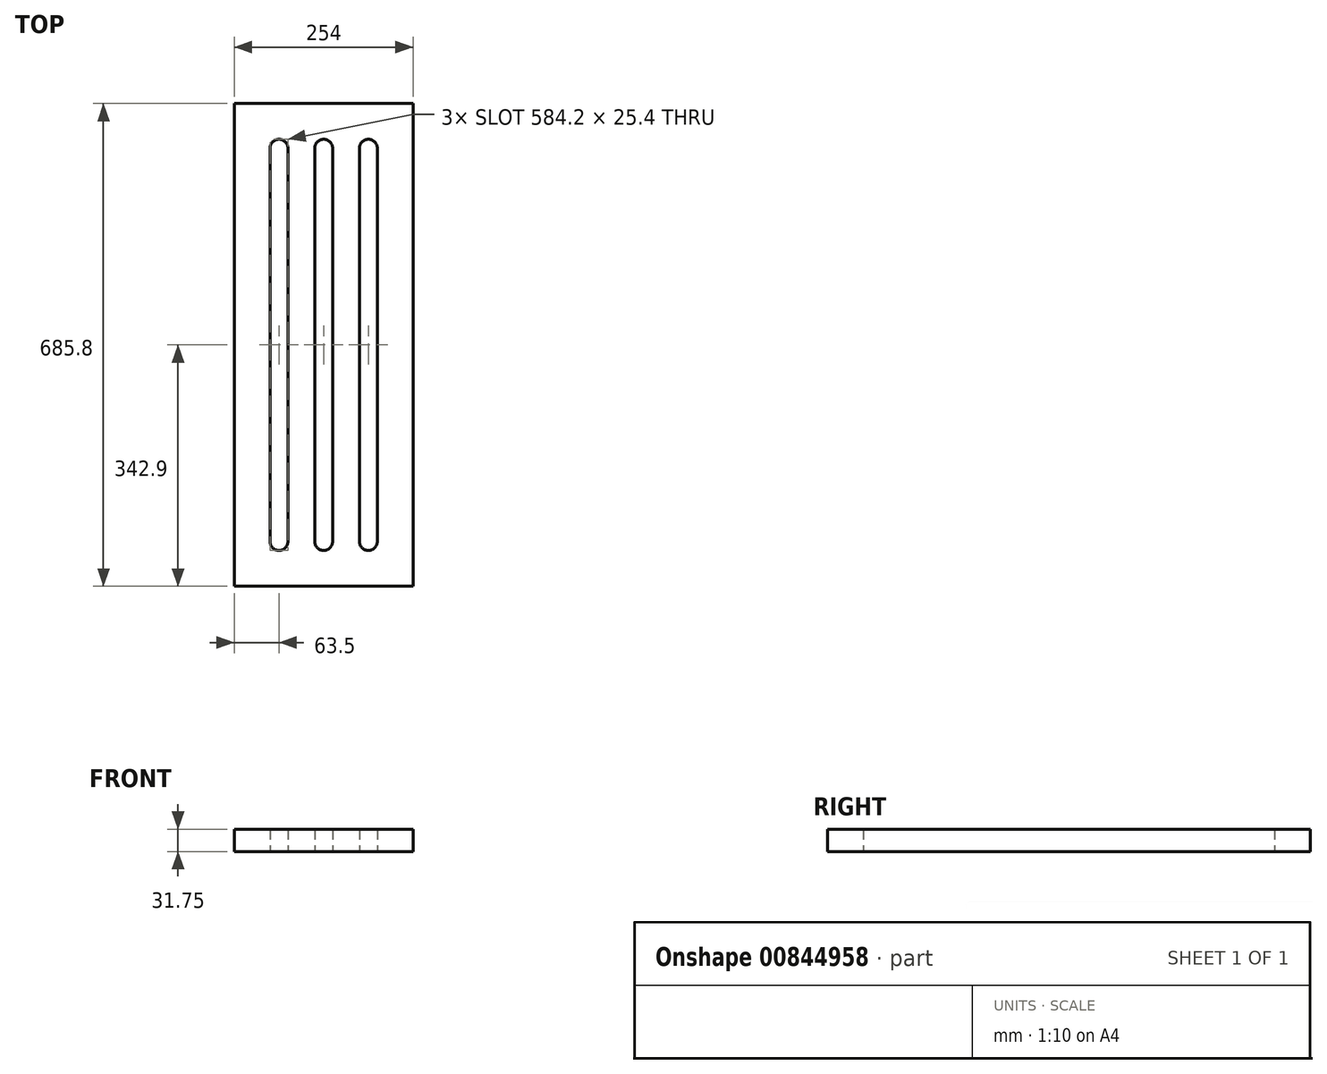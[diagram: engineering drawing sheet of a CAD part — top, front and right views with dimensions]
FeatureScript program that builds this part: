
annotation { "Feature Type Name" : "Feature", "Feature Type Description" : "" }
export const myFeature = defineFeature(function(context is Context, id is Id, definition is map)
    precondition{}
    {
        {
            var Q0;
            Q0=qCreatedBy(makeId("Top.planeOp"),FACE);
            var sketch = newSketch(context, id + "F0", { "sketchPlane" : qUnion([Q0])});
            skLineSegment(sketch, "E0.bottom", {"start": v(127, 342.9) * mm, "end": v(-127, 342.9) * mm});
            skLineSegment(sketch, "E0.top", {"start": v(127, -342.9) * mm, "end": v(-127, -342.9) * mm});
            skLineSegment(sketch, "E0.left", {"start": v(127, 342.9) * mm, "end": v(127, -342.9) * mm});
            skLineSegment(sketch, "E0.right", {"start": v(-127, 342.9) * mm, "end": v(-127, -342.9) * mm});
            skPoint(sketch, "E0.middle", {"position": v(0, 0) * mm});
            skPoint(sketch, "E1", {"position": v(-63.5, 279.4) * mm});
            skPoint(sketch, "E2", {"position": v(63.5, 279.4) * mm});
            skPoint(sketch, "E3", {"position": v(0, 279.4) * mm});
            skPoint(sketch, "E4", {"position": v(-63.5, -279.4) * mm});
            skPoint(sketch, "E5", {"position": v(0, -279.4) * mm});
            skPoint(sketch, "E6", {"position": v(63.5, -279.4) * mm});
            skCircle(sketch, "E7", {"center": v(-63.5, 279.4) * mm, "radius": 12.7 * mm});
            skCircle(sketch, "E8", {"center": v(0, 279.4) * mm, "radius": 12.7 * mm});
            skCircle(sketch, "E9", {"center": v(63.5, 279.4) * mm, "radius": 12.7 * mm});
            skCircle(sketch, "E10", {"center": v(-63.5, -279.4) * mm, "radius": 12.7 * mm});
            skCircle(sketch, "E11", {"center": v(0, -279.4) * mm, "radius": 12.7 * mm});
            skCircle(sketch, "E12", {"center": v(63.5, -279.4) * mm, "radius": 12.7 * mm});
            skLineSegment(sketch, "E13", {"start": v(-76.2, 279.4) * mm, "end": v(-76.2, -279.4) * mm});
            skLineSegment(sketch, "E14", {"start": v(-50.8, 279.4) * mm, "end": v(-50.8, -279.4) * mm});
            skLineSegment(sketch, "E15", {"start": v(-12.7, 279.4) * mm, "end": v(-12.7, -279.4) * mm});
            skLineSegment(sketch, "E16", {"start": v(12.7, 279.4) * mm, "end": v(12.7, -279.4) * mm});
            skLineSegment(sketch, "E17", {"start": v(50.8, 279.4) * mm, "end": v(50.8, -279.4) * mm});
            skLineSegment(sketch, "E18", {"start": v(76.2, 279.4) * mm, "end": v(76.2, -279.4) * mm});
            skSolve(sketch);
        }
        {
            var Q0;
            Q0=qSketchRegion(id+"F0",true);
            extrude(context, id + "F1", {"entities" : qUnion([Q0]), "depth" : 31.75 * mm, "offsetDistance" : 25.4 * mm});
        }
    });
